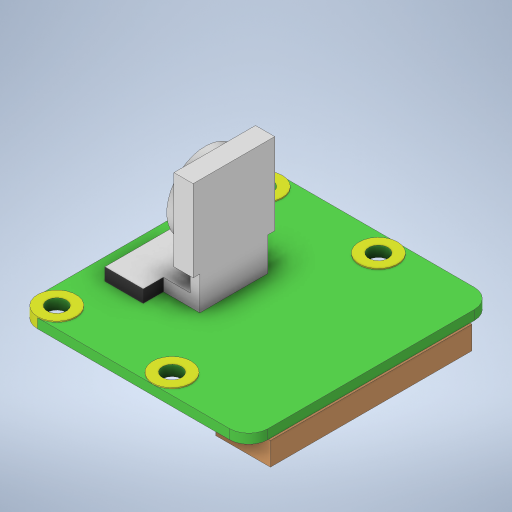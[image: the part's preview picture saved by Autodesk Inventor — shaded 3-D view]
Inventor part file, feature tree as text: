
AUTODESK INVENTOR PART (.ipt)
format: ipt  version: 2023 (Build 270158000, 158)  size: 372,224 bytes
history: native  units: mm
features: extrude x9, sketch x7, other x2, fillet x1, mirror x1, pattern_linear x1
ambient origin geometry x8: Origin, YZ Plane, XZ Plane, XY Plane, X Axis, Y Axis, Z Axis, Center Point
bodies: Body1 (feature_tree)
feature tree (21):
  other  "솔리드1"
  sketch  "스케치1"
  extrude  "돌출1"  Depth=25.5mm
  extrude  "돌출2"  Depth=24.0mm
  extrude  "돌출3"  Depth=8.5mm
  fillet  "모깎기1"  Radius=8.5mm
  mirror  "미러3"
  pattern_linear  "직사각형 패턴1"  Spacing1=17.7mm  [1 undecoded]
  sketch  "스케치2"
  extrude  "돌출7"  Depth=1.0mm
  extrude  "돌출8"  Depth=7.1mm
  extrude  "돌출9"  Depth=4.0mm
  other  "작업 평면1"
  sketch  "스케치7"
  extrude  "돌출10"  Depth=7.0mm
  extrude  "돌출11"  Depth=9.2mm
  extrude  "돌출12"  Depth=2.0mm
  sketch  "스케치4"
  sketch  "스케치5"
  sketch  "스케치6"
  sketch  "스케치8"
note: 1 required parameter value undecoded (feature->parameter linkage not recoverable at this tier; creation-order binding heuristic only, values carry confidence <= 0.55)
